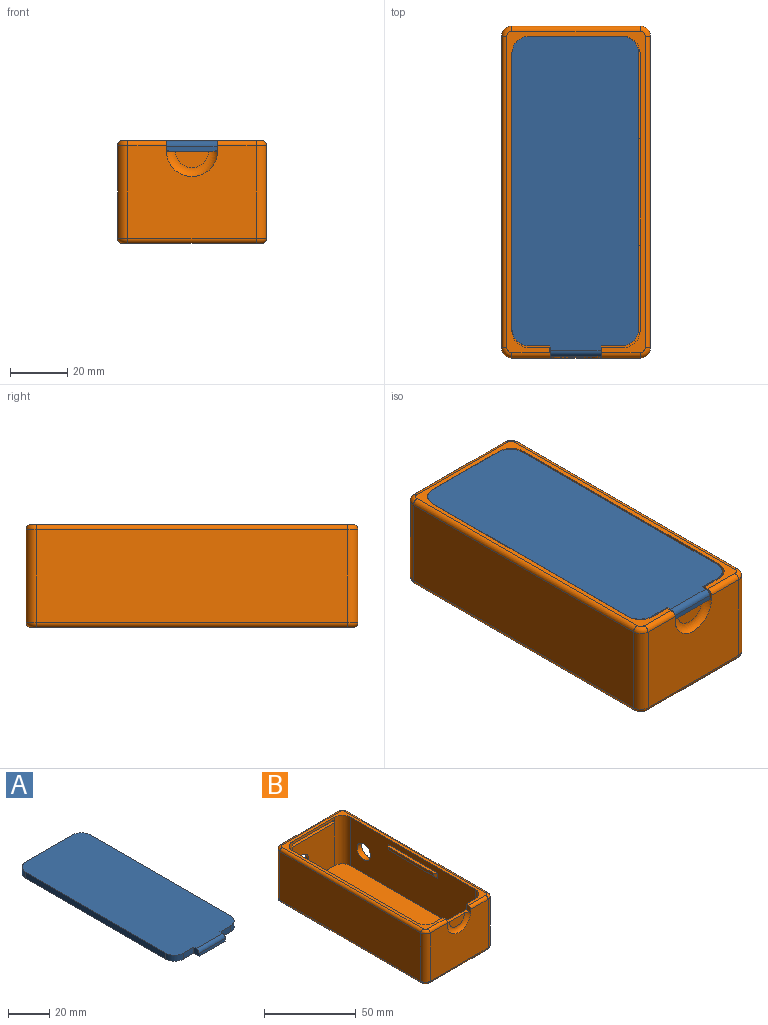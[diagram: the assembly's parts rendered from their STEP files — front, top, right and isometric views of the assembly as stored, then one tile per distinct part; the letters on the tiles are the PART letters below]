
ASSEMBLY  parts=2 mates=1
PART A: 20 faces, bbox 44.3x113.7x3.6 mm
  f0: plane 7.15x3.6mm, normal (0,-1,0), area 25.7mm2, adj f5,f9,f10,f12
  f1: cylinder r=6mm len=6mm, axis (0,0,-1), area 33.9mm2, adj f2,f8,f9,f10,f15
  f2: plane 32.3x1.8mm, normal (0,1,0), area 58.1mm2, adj f1,f3,f9,f14
  f3: cylinder r=6mm len=6mm, axis (0,0,-1), area 33.9mm2, adj f2,f4,f9,f10,f16
  f4: plane 96.31x3.6mm, normal (-1,0,0), area 346.7mm2, adj f3,f5,f9,f10
  f5: cylinder r=6mm len=6mm, axis (0,0,-1), area 33.9mm2, adj f0,f4,f9,f10
  f6: plane 7.15x3.6mm, normal (0,-1,0), area 25.7mm2, adj f7,f9,f10,f11
  f7: cylinder r=6mm len=6mm, axis (0,0,-1), area 33.9mm2, adj f6,f8,f9,f10
  f8: plane 96.31x3.6mm, normal (1,0,0), area 346.7mm2, adj f1,f7,f9,f10
  f9: plane 110x44.3mm, normal (0,0,1), area 4797.4mm2, adj f0,f1,f2,f3,f4,f5,f6,f7
  f10: plane 113.7x44.3mm, normal (0,0,-1), area 4889.8mm2, adj f0,f1,f3,f4,f5,f6,f7,f8
  f11: plane 3.6x3.6mm, normal (1,0,0), area 12.2mm2, adj f6,f9,f10,f13,f18
  f12: plane 3.6x3.6mm, normal (-1,0,0), area 12.2mm2, adj f0,f9,f10,f13,f18
  f13: plane 18x1.7mm, normal (0,-1,0), area 30.6mm2, adj f10,f11,f12,f18
  f14: plane 32.3x1.3mm, normal (0,0,1), area 42mm2, adj f2,f15,f16,f19
  f15: plane 1.8x1.8mm, normal (1,0,0), area 3.2mm2, adj f1,f10,f14,f17,f19
  f16: plane 1.8x1.8mm, normal (-1,0,0), area 3.2mm2, adj f3,f10,f14,f17,f19
  f17: plane 32.3x1.3mm, normal (0,1,0), area 42mm2, adj f10,f15,f16,f19
  f18: cylinder r=1.9mm len=18mm, axis (-1,0,0), area 53.7mm2, adj f9,f11,f12,f13
  f19: cylinder r=0.5mm len=32.3mm, axis (-1,0,0), area 25.4mm2, adj f14,f15,f16,f17
PART B: 62 faces, bbox 52.6x118.1x36 mm
  f0: plane 96.81x32.4mm, normal (1,0,0), area 2998.7mm2, adj f4,f11,f16,f17,f52,f57,f58,f59
  f1: plane 96.81x32.4mm, normal (-1,0,0), area 2912.1mm2, adj f4,f11,f18,f19,f21,f50,f54,f55
  f2: plane 44.8x32.4mm, normal (0,1,0), area 999.1mm2, adj f12,f13,f34,f44,f47
  f3: plane 32.8x1.7mm, normal (0,-1,0), area 55.8mm2, adj f4,f17,f18,f28
  f4: plane 112.4x48.4mm, normal (0,0,1), area 561.6mm2, adj f0,f1,f3,f5,f16,f17,f18,f19
  f5: plane 32.8x32.4mm, normal (0,1,0), area 998.1mm2, adj f4,f11,f16,f19,f22,f23,f24
  f6: plane 44.8x32.4mm, normal (0,-1,0), area 1291.9mm2, adj f14,f15,f22,f24,f30,f38,f41,f61
  f7: plane 32.8x28.7mm, normal (0,-1,0), area 854.9mm2, adj f11,f17,f18,f20,f26
  f8: plane 108.8x32.4mm, normal (1,0,0), area 3438.5mm2, adj f12,f15,f21,f32,f45
  f9: plane 108.8x32.4mm, normal (-1,0,0), area 3525.1mm2, adj f13,f14,f36,f40
  f10: plane 112.4x48.4mm, normal (0,0,-1), area 5437.4mm2, adj f39,f40,f41,f42,f43,f44,f45,f46
  f11: plane 108.8x44.8mm, normal (0,0,1), area 4843.4mm2, adj f0,f1,f5,f7,f16,f17,f18,f19
  f12: cylinder r=3.6mm len=32.4mm, axis (0,0,-1), area 183.2mm2, adj f2,f8,f33,f46
  f13: cylinder r=3.6mm len=32.4mm, axis (0,0,1), area 183.2mm2, adj f2,f9,f35,f42
  f14: cylinder r=3.6mm len=32.4mm, axis (0,0,-1), area 183.2mm2, adj f6,f9,f37,f39
  f15: cylinder r=3.6mm len=32.4mm, axis (0,0,1), area 183.2mm2, adj f6,f8,f31,f43
  f16: cylinder r=6mm len=32.4mm, axis (0,0,1), area 305.2mm2, adj f0,f4,f5,f11
  f17: cylinder r=6mm len=32.4mm, axis (0,0,-1), area 305.2mm2, adj f0,f3,f4,f7,f11,f25
  f18: cylinder r=6mm len=32.4mm, axis (0,0,1), area 305.2mm2, adj f1,f3,f4,f7,f11,f27
  f19: cylinder r=6mm len=32.4mm, axis (0,0,-1), area 305.2mm2, adj f1,f4,f5,f11
  f20: cylinder r=5.25mm len=10.5mm, axis (0,1,0), area 85.8mm2, adj f7,f48
  f21: cylinder r=5.25mm len=10.5mm, axis (1,0,0), area 118.8mm2, adj f1,f8
  f22: plane 3.6x3.6mm, normal (1,0,0), area 12.3mm2, adj f4,f5,f6,f23,f38
  f23: plane 18x3.6mm, normal (0,0,1), area 35.7mm2, adj f5,f22,f24,f60,f61
  f24: plane 3.6x3.6mm, normal (-1,0,0), area 12.3mm2, adj f4,f5,f6,f23,f30
  f25: plane 2.1x2mm, normal (1,0,0), area 4.1mm2, adj f17,f26,f28,f29,f49
  f26: plane 32.8x2.1mm, normal (0,0,1), area 68.9mm2, adj f7,f25,f27,f29
  f27: plane 2.1x2mm, normal (-1,0,0), area 4.1mm2, adj f18,f26,f28,f29,f49
  f28: plane 32.8x1.6mm, normal (0,0,-1), area 52.5mm2, adj f3,f25,f27,f49
  f29: plane 32.8x1.5mm, normal (0,-1,0), area 49.2mm2, adj f25,f26,f27,f49
  f30: cylinder r=1.8mm len=13.4mm, axis (-1,0,0), area 37.9mm2, adj f4,f6,f24,f31
  f31: torus R=1.8mm, axis (0,0,1), area 13.1mm2, adj f4,f15,f30,f32
  f32: cylinder r=1.8mm len=108.8mm, axis (0,-1,0), area 307.6mm2, adj f4,f8,f31,f33
  f33: torus R=1.8mm, axis (0,0,1), area 13.1mm2, adj f4,f12,f32,f34
  f34: cylinder r=1.8mm len=44.8mm, axis (1,0,0), area 126.7mm2, adj f2,f4,f33,f35
  f35: torus R=1.8mm, axis (0,0,1), area 13.1mm2, adj f4,f13,f34,f36
  f36: cylinder r=1.8mm len=108.8mm, axis (0,1,0), area 307.6mm2, adj f4,f9,f35,f37
  f37: torus R=1.8mm, axis (0,0,1), area 13.1mm2, adj f4,f14,f36,f38
  f38: cylinder r=1.8mm len=13.4mm, axis (-1,0,0), area 37.9mm2, adj f4,f6,f22,f37
  f39: torus R=1.8mm, axis (0,0,1), area 13.1mm2, adj f10,f14,f40,f41
  f40: cylinder r=1.8mm len=108.8mm, axis (0,-1,0), area 307.6mm2, adj f9,f10,f39,f42
  f41: cylinder r=1.8mm len=44.8mm, axis (1,0,0), area 126.7mm2, adj f6,f10,f39,f43
  f42: torus R=1.8mm, axis (0,0,1), area 13.1mm2, adj f10,f13,f40,f44
  f43: torus R=1.8mm, axis (0,0,1), area 13.1mm2, adj f10,f15,f41,f45
  f44: cylinder r=1.8mm len=44.8mm, axis (-1,0,0), area 126.7mm2, adj f2,f10,f42,f46
  f45: cylinder r=1.8mm len=108.8mm, axis (0,1,0), area 307.6mm2, adj f8,f10,f43,f46
  f46: torus R=1.8mm, axis (0,0,1), area 13.1mm2, adj f10,f12,f44,f45
  f47: cylinder r=12mm len=24mm, axis (0,1,0), area 75.4mm2, adj f2,f48
  f48: plane 24x24mm, normal (0,1,0), area 365.8mm2, adj f20,f47
  f49: cylinder r=0.5mm len=32.8mm, axis (-1,0,0), area 25.8mm2, adj f25,f27,f28,f29
  f50: plane 38.28x1.8mm, normal (0,0,1), area 65.7mm2, adj f1,f51,f54,f56
  f51: plane 34.68x1.8mm, normal (-1,0,0), area 62.4mm2, adj f50,f54,f55,f56
  f52: plane 38.28x1.8mm, normal (0,0,1), area 65.7mm2, adj f0,f53,f57,f59
  f53: plane 34.68x1.8mm, normal (1,0,0), area 62.4mm2, adj f52,f57,f58,f59
  f54: plane 3.6x1.8mm, normal (-0.71,0.71,0), area 6.9mm2, adj f1,f50,f51,f55
  f55: plane 38.28x1.8mm, normal (-0.71,0,-0.71), area 92.9mm2, adj f1,f51,f54,f56
  f56: plane 3.6x1.8mm, normal (-0.71,-0.71,0), area 6.9mm2, adj f1,f50,f51,f55
  f57: plane 3.6x1.8mm, normal (0.71,-0.71,0), area 6.9mm2, adj f0,f52,f53,f58
  f58: plane 38.28x1.8mm, normal (0.71,0,-0.71), area 92.9mm2, adj f0,f53,f57,f59
  f59: plane 3.6x1.8mm, normal (0.71,0.71,0), area 6.9mm2, adj f0,f52,f53,f58
  f60: plane 11.76x5.88mm, normal (0,-1,0), area 54.4mm2, adj f23,f61
  f61: torus R=5.88mm, axis (0,1,0), area 90mm2, adj f6,f23,f60
PLACE A t=(34.26,21.24,1.45)mm
PLACE B t=(34.51,20.94,-30.85)mm
MATE fastened B.f26 <-> A.f10  axis (0,0,1) through (18.11,77.44,1.45)mm
